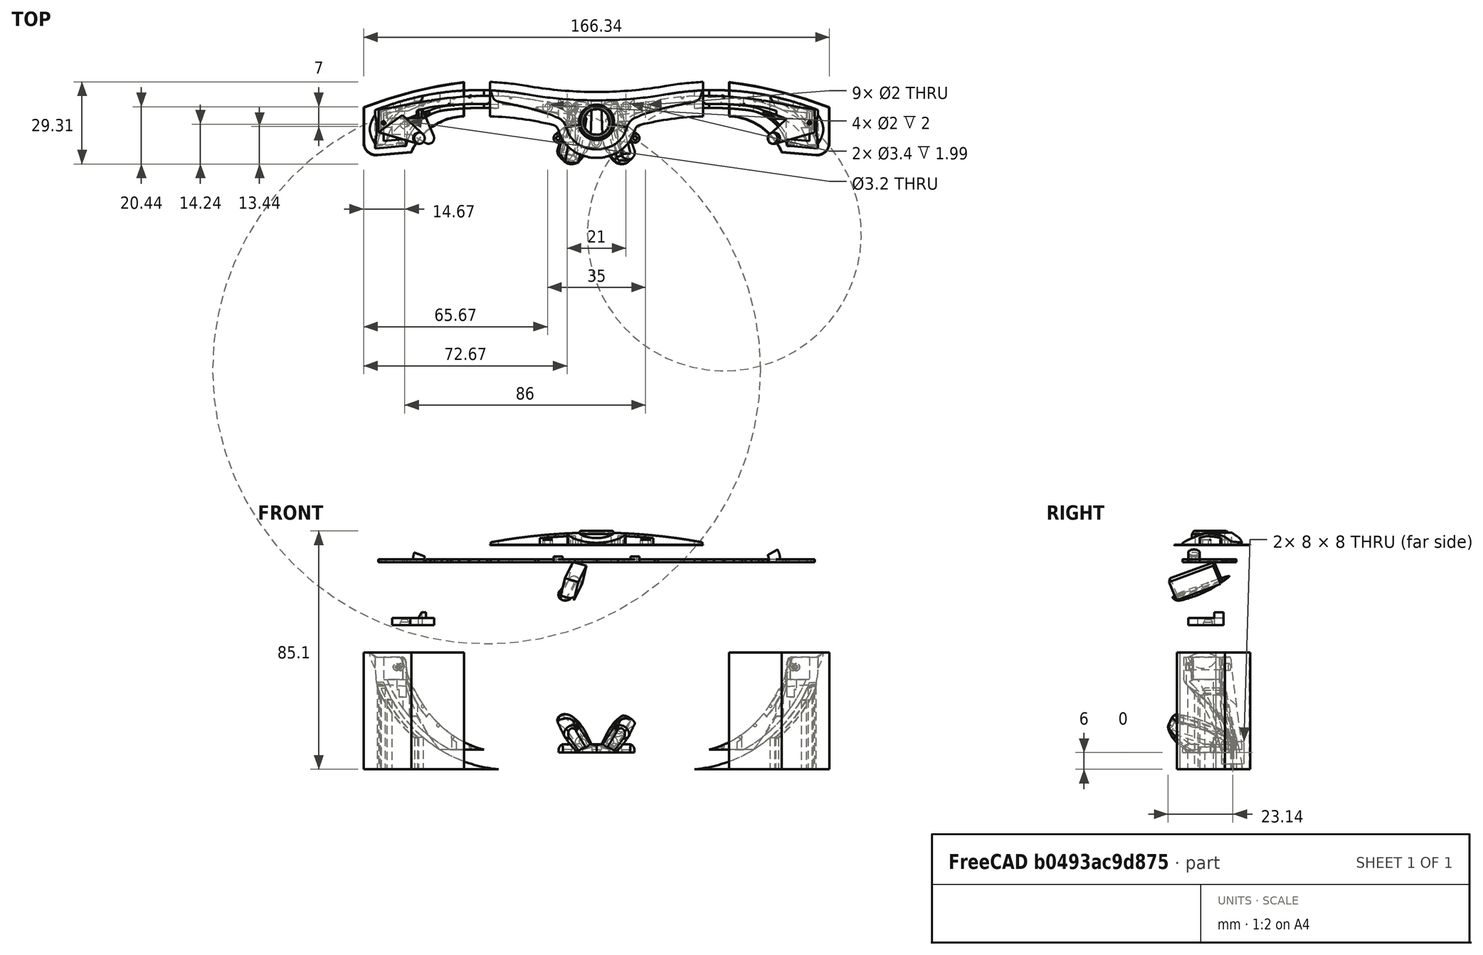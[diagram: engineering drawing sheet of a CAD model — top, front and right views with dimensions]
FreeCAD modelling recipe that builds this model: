
FCSTD DOCUMENT  (FreeCAD 0.14R3700 (Git))
Label: frame12
License: CC-BY 3.0
LicenseURL: http://creativecommons.org/licenses/by/3.0/
objects: Sketcher::SketchObject×44, Part::Extrusion×40, Part::MultiFuse×40, Part::Cut×33, Part::Box×23, Part::MultiCommon×16, Part::Sphere×14, Part::Cylinder×13, Part::FeaturePython×10, Part::Mirroring×9, Part::Loft×8, Part::Feature×7, Part::Fillet×7, PartDesign::Pad×6, Part::Offset×4, Mesh::Feature×4, PartDesign::Revolution×2, Part::Thickness×1
note: 285 computed .brp shape members not serialized (recipe doc carries the construction recipe); baked Part::Feature solids carry a one-line shape summary decoded from their .brp

FEATURE [Sketcher::SketchObject] Sketch001
  sketch-geometry (15):
    g0: ArcOfCircle CenterX=-40.8218 CenterY=-97.0566 CenterZ=0 NormalX=0 NormalY=0 NormalZ=1 Radius=107.874 StartAngle=1.32625 EndAngle=1.69394
    g1: ArcOfCircle CenterX=-42.1655 CenterY=-80.3985 CenterZ=0 NormalX=0 NormalY=0 NormalZ=1 Radius=97.5538 StartAngle=1.39785 EndAngle=1.92498
    g2: LineSegment [constr] StartX=-80 StartY=19.6499 StartZ=0 EndX=80 EndY=19.6499 EndZ=0
    g3: Circle [constr] CenterX=0 CenterY=6 CenterZ=0 NormalX=0 NormalY=0 NormalZ=1 Radius=5.2
    g4: GeomPoint [constr] X=-76 Y=11.1 Z=0
    g5: LineSegment StartX=0 StartY=13.5 StartZ=0 EndX=0 EndY=-4 EndZ=0
    g6: Circle [constr] CenterX=-7.5 CenterY=3.5 CenterZ=0 NormalX=0 NormalY=0 NormalZ=1 Radius=1.25
    g7: LineSegment [constr] StartX=-7.9694 StartY=13.5 StartZ=0 EndX=9.38441 EndY=13.5 EndZ=0
    g8: ArcOfCircle CenterX=-16.005 CenterY=2.39295 CenterZ=0 NormalX=0 NormalY=0 NormalZ=1 Radius=5.3743 StartAngle=0.264318 EndAngle=1.32625
    g9: ArcOfCircle CenterX=-0.822877 CenterY=6.50201 CenterZ=0 NormalX=0 NormalY=0 NormalZ=1 Radius=10.3541 StartAngle=3.40591 EndAngle=4.45086
    g10: ArcOfCircle CenterX=0.329777 CenterY=10.8084 CenterZ=0 NormalX=0 NormalY=0 NormalZ=1 Radius=14.8121 StartAngle=4.45086 EndAngle=4.69012
    g11: ArcOfCircle CenterX=1.76172e-06 CenterY=160.97 CenterZ=0 NormalX=0 NormalY=0 NormalZ=1 Radius=147.47 StartAngle=4.53944 EndAngle=4.71239
    g12: LineSegment StartX=-76 StartY=11.1 StartZ=0 EndX=-76 EndY=-3.4 EndZ=0
    g13: ArcOfCircle CenterX=-52.0663 CenterY=-6.2076 CenterZ=0 NormalX=0 NormalY=0 NormalZ=1 Radius=16.3313 StartAngle=1.69394 EndAngle=2.92806
    g14: LineSegment StartX=-76 StartY=-3.4 StartZ=0 EndX=-68.0267 EndY=-2.74684 EndZ=0
  constraints (44):
    c: Horizontal(g2)
    c: Distance(g2) = 160
    c: Symmetric(g2,g2,g-2)
    c: Radius(g3) = 5.2
    c: PointOnObject(g3,g-2)
    c: DistanceY(g-1,g3) = 6
    c: Vertical(g5)
    c: PointOnObject(g5,g-2)
    c: Distance(g5,g3) = 7.5
    c: Radius(g6) = 1.25
    c: Distance(g6,g5) = 7.5
    c: Horizontal(g7)
    c: PointOnObject(g5,g7)
    c: Coincident(g8,g0)
    c: Coincident(g9,g8)
    c: Tangent(g9,g8)
    c: Coincident(g10,g9)
    c: Tangent(g10,g9)
    c: Coincident(g10,g5)
    c: Coincident(g11,g1)
    c: Tangent(g11,g1)
    c: Tangent(g8,g0)
    c: Coincident(g1,g4)
    c: DistanceY(g12) = -14.5
    c: DistanceY(g5,g3) = 10
    c: Coincident(g1,g12)
    c: Coincident(g11,g5)
    c: Coincident(g13,g0)
    c: Tangent(g0,g13)
    c: DistanceX(g0) = -14.7038
    c: DistanceY(g0) = 7.60735
    c: Coincident(g14,g12)
    c: Coincident(g13,g14)
    c: Distance(g14) = 8
    c: DistanceX(g-2,g1) = -76
    c: DistanceY(g6,g3) = 2.5
    c: DistanceY(g1) = 15.7
    c: Tangent(g7,g11)
    c: DistanceX(g0) = -54.0724
    c: DistanceY(g0) = 10
    c: DistanceY(g9) = -3.5
    c: DistanceX(g9) = -3.5
    c: Vertical(g12)
    c: DistanceY(g12) = -3.4
FEATURE [Part::Extrusion] Extrude003
  Base = -> Sketch001
  Dir = (0,0,40)
  Solid = true
FEATURE [Sketcher::SketchObject] Sketch
  ExternalGeometry = -> [Extrude003]
  Placement = pos=(0,0,40) rot=(0,0,1;0rad)
  Support = -> Extrude003 [Face12]
  sketch-geometry (17):
    g0: ArcOfCircle CenterX=-41.618 CenterY=-95.1729 CenterZ=0 NormalX=0 NormalY=0 NormalZ=1 Radius=107.432 StartAngle=1.31635 EndAngle=1.68162
    g1: ArcOfCircle CenterX=-39.255 CenterY=-82.6924 CenterZ=0 NormalX=0 NormalY=0 NormalZ=1 Radius=97.8262 StartAngle=1.39348 EndAngle=1.70145
    g2: LineSegment [constr] StartX=-80 StartY=19.6499 StartZ=0 EndX=80 EndY=19.6499 EndZ=0
    g3: Circle [constr] CenterX=0 CenterY=6 CenterZ=0 NormalX=0 NormalY=0 NormalZ=1 Radius=5.2
    g4: LineSegment StartX=0 StartY=12 StartZ=0 EndX=0 EndY=-3 EndZ=0
    g5: Circle [constr] CenterX=-7.5 CenterY=4 CenterZ=0 NormalX=0 NormalY=0 NormalZ=1 Radius=1.25
    g6: ArcOfCircle CenterX=-16.4199 CenterY=1.71051 CenterZ=0 NormalX=0 NormalY=0 NormalZ=1 Radius=7.32535 StartAngle=0.257118 EndAngle=1.31635
    g7: ArcOfCircle CenterX=-1.30056 CenterY=5.68595 CenterZ=0 NormalX=0 NormalY=0 NormalZ=1 Radius=8.30788 StartAngle=3.39871 EndAngle=4.3949
    g8: ArcOfCircle CenterX=1.44145 CenterY=14.0305 CenterZ=0 NormalX=0 NormalY=0 NormalZ=1 Radius=17.0914 StartAngle=4.3949 EndAngle=4.62795
    g9: LineSegment StartX=-76 StartY=9.05149 StartZ=0 EndX=-76 EndY=-0.948515 EndZ=0
    g10: ArcOfCircle CenterX=-51.3984 CenterY=-7.28562 CenterZ=0 NormalX=0 NormalY=0 NormalZ=1 Radius=19.0022 StartAngle=1.68162 EndAngle=2.76947
    g11: LineSegment StartX=-76 StartY=-0.948515 StartZ=0 EndX=-69.1 EndY=-0.376553 EndZ=0
    g12: LineSegment StartX=-76 StartY=9.05149 StartZ=0 EndX=-69 EndY=9.63174 EndZ=0
    g13: ArcOfCircle CenterX=-45.6302 CenterY=-34.1756 CenterZ=0 NormalX=0 NormalY=0 NormalZ=1 Radius=48.8923 StartAngle=1.70145 EndAngle=2.01768
    g14: LineSegment StartX=-4 StartY=12 StartZ=0 EndX=0 EndY=12 EndZ=0
    g15: ArcOfCircle CenterX=-4.00001 CenterY=114.05 CenterZ=0 NormalX=0 NormalY=0 NormalZ=1 Radius=102.05 StartAngle=4.53508 EndAngle=4.71239
    g16: LineSegment StartX=-66.7595 StartY=9.91534 StartZ=0 EndX=-69 EndY=9.63174 EndZ=0
  constraints (51):
    c: Horizontal(g2)
    c: Distance(g2) = 160
    c: Symmetric(g2,g2,g-2)
    c: Radius(g3) = 5.2
    c: PointOnObject(g3,g-2)
    c: DistanceY(g-1,g3) = 6
    c: Vertical(g4)
    c: PointOnObject(g4,g-2)
    c: Distance(g4,g3) = 6
    c: Radius(g5) = 1.25
    c: Distance(g5,g4) = 7.5
    c: Coincident(g6,g0)
    c: Coincident(g7,g6)
    c: Tangent(g7,g6)
    c: Coincident(g8,g7)
    c: Tangent(g8,g7)
    c: Tangent(g6,g0)
    c: DistanceY(g9) = -10
    c: DistanceY(g4,g3) = 9
    c: Coincident(g10,g0)
    c: Tangent(g0,g10)
    c: Coincident(g11,g9)
    c: Coincident(g10,g11)
    c: Distance(g10,g-4) = 2.45
    c: Coincident(g12,g9)
    c: DistanceX(g0) = -14.576
    c: DistanceY(g0) = 8.8
    c: Coincident(g8,g4)
    c: DistanceY(g0) = 11.6
    c: Coincident(g13,g1)
    c: Tangent(g13,g1)
    c: PointOnObject(g9,g-3)
    c: PointOnObject(g9,g-3)
    c: DistanceX(g10) = -69.1
    c: DistanceY(g1) = 14.3
    c: DistanceX(g1) = -52
    c: Coincident(g15,g1)
    c: Coincident(g15,g14)
    c: Tangent(g15,g14)
    c: Horizontal(g14)
    c: Coincident(g14,g4)
    c: Tangent(g15,g1)
    c: DistanceX(g14) = -4
    c: DistanceY(g1) = 13.6
    c: DistanceX(g1) = -22
    c: DistanceX(g0) = -53.5
    c: Coincident(g16,g13)
    c: Coincident(g16,g12)
    c: Radius(g0) = 107.432
    c: DistanceX(g12) = -69
    c: Parallel(g12,g11)
FEATURE [Part::Extrusion] Extrude002
  Base = -> Sketch
  Dir = (0,0,-40)
  Solid = true
FEATURE [Sketcher::SketchObject] Sketch002
  Placement = pos=(0,-15,0) rot=(1,0,0;1.5708rad)
  sketch-geometry (12):
    g0: LineSegment StartX=0 StartY=40 StartZ=0 EndX=0 EndY=34 EndZ=0
    g1: LineSegment [constr] StartX=0 StartY=40 StartZ=0 EndX=0 EndY=0 EndZ=0
    g2: LineSegment [constr] StartX=-76 StartY=0 StartZ=0 EndX=-76 EndY=40 EndZ=0
    g3: LineSegment [constr] StartX=-60 StartY=34 StartZ=0 EndX=-60 EndY=29 EndZ=0
    g4: LineSegment StartX=-35 StartY=40 StartZ=0 EndX=0 EndY=40 EndZ=0
    g5: ArcOfCircle CenterX=-29.5232 CenterY=-9.43659 CenterZ=0 NormalX=0 NormalY=0 NormalZ=1 Radius=50 StartAngle=2.27585 EndAngle=2.76395
    g6: ArcOfCircle CenterX=-30.8281 CenterY=-2.13188 CenterZ=0 NormalX=0 NormalY=0 NormalZ=1 Radius=36.3719 StartAngle=1.68575 EndAngle=2.3997
    g7: ArcOfCircle CenterX=-27.7253 CenterY=-4.97584 CenterZ=0 NormalX=0 NormalY=0 NormalZ=1 Radius=40.5809 StartAngle=2.3997 EndAngle=3.01867
    g8: ArcOfCircle CenterX=-30.4815 CenterY=-8.31047 CenterZ=0 NormalX=0 NormalY=0 NormalZ=1 Radius=48.5213 StartAngle=1.66406 EndAngle=2.27585
    g9: LineSegment StartX=-35 StartY=34 StartZ=0 EndX=0 EndY=34 EndZ=0
    g10: LineSegment StartX=-76 StartY=0 StartZ=0 EndX=-68 EndY=0 EndZ=0
    g11: LineSegment StartX=-76 StartY=9 StartZ=0 EndX=-76 EndY=0 EndZ=0
  constraints (33):
    c: Distance(g0,g0) = 6
    c: Vertical(g1)
    c: Vertical(g2)
    c: Coincident(g1,g-1)
    c: DistanceY(g2) = 40
    c: PointOnObject(g0,g1)
    c: DistanceY(g3) = -5
    c: Vertical(g3)
    c: Distance(g4) = 35
    c: Coincident(g7,g6)
    c: Tangent(g7,g6)
    c: Horizontal(g4)
    c: Coincident(g4,g0)
    c: DistanceY(g-1,g0) = 40
    c: Vertical(g0)
    c: Coincident(g4,g8)
    c: DistanceX(g2) = -76
    c: Coincident(g8,g5)
    c: Tangent(g8,g5)
    c: Coincident(g9,g6)
    c: Coincident(g9,g0)
    c: Horizontal(g9)
    c: Equal(g9,g4)
    c: PointOnObject(g7,g-1)
    c: Radius(g5) = 50
    c: PointOnObject(g2,g-1)
    c: Coincident(g10,g2)
    c: Coincident(g10,g7)
    c: Distance(g10) = 8
    c: DistanceY(g5) = 9
    c: Coincident(g11,g5)
    c: Coincident(g11,g2)
    c: Vertical(g11)
FEATURE [Part::Extrusion] Extrude
  Base = -> Sketch002
  Dir = (0,40,0)
  Solid = true
FEATURE [Part::MultiCommon] Common001  label="trunk"
  Shapes = -> [Extrude,Extrude003]
FEATURE [Part::Extrusion] Extrude001
  Base = -> Sketch002
  Dir = (0,40,0)
  Placement = pos=(1,0,-1.5) rot=(0,0,1;0rad)
  Solid = true
FEATURE [Part::MultiCommon] Common  label="trunk inner"
  Shapes = -> [Extrude001,Extrude002]
FEATURE [Part::Cut] Cut  label="trunk002"
  Base = -> Common001
  Tool = -> Common
FEATURE [Sketcher::SketchObject] Sketch004
  Placement = pos=(-46.8224,0,73.5) rot=(0,-1,0;1.0472rad)
  sketch-geometry (3):
    g0: ArcOfCircle CenterX=-34.7524 CenterY=-32.9515 CenterZ=0 NormalX=0 NormalY=0 NormalZ=1 Radius=49.1722 StartAngle=1.79408 EndAngle=2.63591
    g1: LineSegment StartX=-77.7704 StartY=-9.13213 StartZ=0 EndX=-45.641 EndY=-9.13213 EndZ=0
    g2: LineSegment StartX=-45.641 StartY=15 StartZ=0 EndX=-45.641 EndY=-9.13213 EndZ=0
  constraints (8):
    c: Coincident(g1,g0)
    c: Horizontal(g1)
    c: Coincident(g2,g0)
    c: Coincident(g2,g1)
    c: Vertical(g2)
    c: DistanceX(g0) = -77.7704
    c: DistanceY(g0) = -9.13213
    c: DistanceY(g0) = 15
FEATURE [Part::Extrusion] Extrude005  label="sideCut"
  Base = -> Sketch004
  Dir = (30,0,0)
  Solid = true
FEATURE [Part::Box] Box  label="Cube002"
  Height = 21
  Length = 18
  Placement = pos=(-78,3.8,11) rot=(0,0,1;0rad)
  Width = 14
FEATURE [Part::Box] Box002  label="Cube022"
  Height = 13
  Length = 11.5
  Placement = pos=(-75,-1,8) rot=(0,0,1;0rad)
  Width = 8
FEATURE [Part::Box] Box003  label="Cube023"
  Height = 29
  Length = 17
  Placement = pos=(-75,-1.2,6) rot=(0,0,1;0rad)
  Width = 12
FEATURE [Part::Box] Box004  label="Cube017"
  Height = 15
  Length = 8
  Placement = pos=(-69.7,-0.95,-0.8) rot=(0,0,1;0rad)
  Width = 10
FEATURE [Part::Box] Box005  label="Cube032"
  Height = 15
  Length = 15
  Placement = pos=(-79.5,-0.95,-7) rot=(0,0,1;0rad)
  Width = 10
FEATURE [Part::Box] Box006  label="Cube033"
  Height = 12.5
  Length = 10
  Placement = pos=(-70.5,-0.95,-1) rot=(0,0,1;0rad)
  Width = 10
FEATURE [Part::MultiFuse] Fusion003
  Placement = pos=(-0.285398,6.6,0) rot=(0,0,1;0.087266rad)
  Shapes = -> [Box004,Box005,Box006]
FEATURE [Part::Cut] Cut010  label="trunk003"
  Base = -> Cut
  Tool = -> Fusion003
FEATURE [Sketcher::SketchObject] Sketch015
  Placement = pos=(-46.8224,0,71.5321) rot=(0,-1,0;1.0472rad)
  sketch-geometry (3):
    g0: ArcOfCircle CenterX=-32.5352 CenterY=-52.0195 CenterZ=0 NormalX=0 NormalY=0 NormalZ=1 Radius=62.8287 StartAngle=1.65242 EndAngle=2.37985
    g1: LineSegment StartX=-78 StartY=-8.65601 StartZ=0 EndX=-37.6576 EndY=-8.65601 EndZ=0
    g2: LineSegment StartX=-37.6576 StartY=10.6 StartZ=0 EndX=-37.6576 EndY=-8.65601 EndZ=0
  constraints (8):
    c: Coincident(g1,g0)
    c: Horizontal(g1)
    c: Coincident(g2,g0)
    c: Coincident(g2,g1)
    c: Vertical(g2)
    c: DistanceX(g0) = -37.6576
    c: DistanceY(g0) = 10.6
    c: DistanceX(g0) = -78
FEATURE [Part::Extrusion] Extrude008
  Base = -> Sketch015
  Dir = (20,0,0)
  Placement = pos=(0,1.5,0) rot=(0,0,1;0rad)
  Solid = true
FEATURE [Part::Extrusion] Extrude009
  Base = -> Sketch015
  Dir = (30,0,0)
  Solid = true
FEATURE [Part::MultiCommon] Common003
  Shapes = -> [Box003,Extrude008]
FEATURE [Part::MultiFuse] Fusion004  label="sideInner"
  Shapes = -> [Box002,Common003]
FEATURE [Part::MultiCommon] Common004  label="sideInner001"
  Shapes = -> [Fusion004,Common001]
FEATURE [Part::Box] Box007  label="Cube037"
  Height = 4
  Length = 9.3
  Placement = pos=(-8.3,-3,35) rot=(0,0,1;0rad)
  Width = 4
FEATURE [Part::Cylinder] Cylinder
  Angle = 360
  Height = 6.5
  Placement = pos=(-9,10,31) rot=(0,0,1;0rad)
  Radius = 1
FEATURE [Part::Box] Box008  label="Cube038"
  Height = 4
  Length = 4
  Placement = pos=(-13,10.5,35) rot=(0,0,1;0rad)
  Width = 2
FEATURE [Part::Cylinder] Cylinder001
  Angle = 360
  Height = 4
  Placement = pos=(-11,10.5,35) rot=(0,0,1;0rad)
  Radius = 2
FEATURE [Part::MultiFuse] Fusion005
  Placement = pos=(2,-0.5,0) rot=(0,0,1;0rad)
  Shapes = -> [Cylinder001,Box008]
FEATURE [Part::Cut] Cut011
  Base = -> Fusion005
  Placement = pos=(-1.5,1.2,0) rot=(0,0,1;0rad)
  Tool = -> Cylinder
FEATURE [Part::MultiCommon] Common005
  Shapes = -> [Box007,Common]
FEATURE [Part::Cylinder] Cylinder002
  Angle = 360
  Height = 12.5
  Placement = pos=(0,5.8,32) rot=(0,0,1;0rad)
  Radius = 5.3
FEATURE [Part::Box] Box009  label="Cube024"
  Height = 2
  Length = 8.4
  Placement = pos=(-4.2,1.6,32) rot=(0,0,1;0rad)
  Width = 8.4
FEATURE [Part::MultiFuse] Fusion006  label="camera"
  Shapes = -> [Cylinder002,Box009]
FEATURE [Part::MultiFuse] Fusion007  label="inner"
  Shapes = -> [Cut011,Common005]
FEATURE [Sketcher::SketchObject] Sketch016
  Placement = pos=(0,0,34) rot=(1,0,0;3.14159rad)
  sketch-geometry (7):
    g0: ArcOfCircle CenterX=-13.75 CenterY=0 CenterZ=0 NormalX=0 NormalY=0 NormalZ=1 Radius=1.6 StartAngle=1.51787 EndAngle=4.02214
    g1: LineSegment StartX=-14.7688 StartY=-1.23374 StartZ=0 EndX=-8.68396 EndY=-6.25827 EndZ=0
    g2: LineSegment StartX=-13.6654 StartY=1.59776 StartZ=0 EndX=-7.7 EndY=1.28174 EndZ=0
    g3: ArcOfCircle CenterX=-0.545251 CenterY=-6.72046 CenterZ=0 NormalX=0 NormalY=0 NormalZ=1 Radius=10.7343 StartAngle=1.51998 EndAngle=2.30034
    g4: ArcOfCircle CenterX=0 CenterY=-6 CenterZ=0 NormalX=0 NormalY=0 NormalZ=1 Radius=6 StartAngle=1.5708 EndAngle=3.18465
    g5: LineSegment StartX=-8.68396 StartY=-6.25827 StartZ=0 EndX=-5.99444 EndY=-6.25827 EndZ=0
    g6: LineSegment StartX=0 StartY=4 StartZ=0 EndX=0 EndY=0 EndZ=0
  constraints (21):
    c: DistanceY(g0) = 0
    c: Radius(g0) = 1.6
    c: DistanceX(g0) = -13.75
    c: Coincident(g1,g0)
    c: Coincident(g2,g0)
    c: Tangent(g2,g0)
    c: Tangent(g1,g0)
    c: Coincident(g3,g2)
    c: PointOnObject(g3,g-2)
    c: DistanceY(g3) = 4
    c: PointOnObject(g4,g-2)
    c: DistanceY(g4) = -6
    c: Radius(g4) = 6
    c: PointOnObject(g4,g-2)
    c: Coincident(g5,g1)
    c: Coincident(g5,g4)
    c: Horizontal(g5)
    c: Coincident(g6,g3)
    c: Coincident(g6,g-1)
    c: DistanceX(g2) = -7.7
    c: DistanceY(g2) = 1.28174
FEATURE [Part::Cylinder] Cylinder004
  Angle = 360
  Height = 2
  Placement = pos=(-13.75,0,34) rot=(0,0,1;0rad)
  Radius = 1.6
FEATURE [Part::Cylinder] Cylinder005
  Angle = 360
  Height = 4
  Placement = pos=(-13.75,0,32.6) rot=(0,0,1;0rad)
  Radius = 0.7
FEATURE [Part::Extrusion] Extrude010  label="right holder"
  Base = -> Sketch016
  Dir = (0,0,1)
  Solid = true
FEATURE [Part::MultiFuse] Fusion009  label="rightHolder"
  Shapes = -> [Extrude010,Cylinder004]
FEATURE [Part::Cut] Cut012  label="rightHolder001"
  Base = -> Fusion009
  Tool = -> Cylinder005
FEATURE [Part::Sphere] Sphere
  Angle1 = -90
  Angle2 = 90
  Angle3 = 360
  Placement = pos=(-51.3628,11.8412,28.4927) rot=(1,0,0;1.5708rad)
  Radius = 0.55
FEATURE [Part::Sphere] Sphere001
  Angle1 = -90
  Angle2 = 90
  Angle3 = 360
  Placement = pos=(-21.3095,10.3221,34.5) rot=(1,0,0;1.5708rad)
  Radius = 0.55
FEATURE [Part::Sphere] Sphere002
  Angle1 = -90
  Angle2 = 90
  Angle3 = 360
  Placement = pos=(-38.3844,12.2073,33.9575) rot=(1,0,0;1.5708rad)
  Radius = 0.55
FEATURE [Part::Sphere] Sphere003
  Angle1 = -90
  Angle2 = 90
  Angle3 = 360
  Placement = pos=(-30.6467,14.7543,34.5) rot=(1,0,0;1.5708rad)
  Radius = 0.55
FEATURE [Part::Sphere] Sphere004
  Angle1 = -90
  Angle2 = 90
  Angle3 = 360
  Placement = pos=(-45.0432,14.9736,31.8897) rot=(1,0,0;1.5708rad)
  Radius = 0.55
FEATURE [Part::Sphere] Sphere006
  Angle1 = -90
  Angle2 = 90
  Angle3 = 360
  Placement = pos=(-56.5763,13.5545,24.2608) rot=(1,0,0;1.5708rad)
  Radius = 0.55
FEATURE [Part::Sphere] Sphere007
  Angle1 = -90
  Angle2 = 90
  Angle3 = 360
  Placement = pos=(-62.1328,11.9954,17.4689) rot=(1,0,0;1.5708rad)
  Radius = 0.55
FEATURE [Part::Box] Box010  label="Cube015"
  Height = 8
  Length = 11
  Placement = pos=(-76.9115,-1.07712,-5.23794e-07) rot=(-0.030761,0.706774,0.70677;0.123394rad)
  Width = 10
FEATURE [Part::FeaturePython] Facebinder  # WARN: FeaturePython — macro-defined, semantics opaque (R4)
  Faces = -> [Common001]
FEATURE [Part::Extrusion] Extrude011  label="side"
  Base = -> Facebinder
  Dir = (-3,-1,0)
  Solid = true
FEATURE [Part::Cut] Cut013  label="side001"
  Base = -> Extrude011
  Tool = -> Extrude005
FEATURE [Part::Cut] Cut014  label="side002"
  Base = -> Extrude011
  Placement = pos=(1.2,-1,0) rot=(0,0,1;0rad)
  Tool = -> Extrude005
FEATURE [Part::MultiCommon] Common006
  Shapes = -> [Cut014,Box]
FEATURE [Sketcher::SketchObject] Sketch017
  Placement = pos=(-0.229946,2.807,0) rot=(0.998332,0.040823,0.040823;1.57247rad)
  sketch-geometry (4):
    g0: LineSegment StartX=-71.1534 StartY=16.0049 StartZ=0 EndX=-84.6914 EndY=16.0049 EndZ=0
    g1: LineSegment StartX=-84.6914 StartY=16.0049 StartZ=0 EndX=-84.6914 EndY=-1.48622 EndZ=0
    g2: LineSegment StartX=-84.6914 StartY=-1.48622 StartZ=0 EndX=-71.1534 EndY=-1.48622 EndZ=0
    g3: LineSegment StartX=-71.1534 StartY=-1.48622 StartZ=0 EndX=-71.1534 EndY=16.0049 EndZ=0
  constraints (8):
    c: Coincident(g0,g1)
    c: Coincident(g1,g2)
    c: Coincident(g2,g3)
    c: Coincident(g3,g0)
    c: Horizontal(g0)
    c: Horizontal(g2)
    c: Vertical(g1)
    c: Vertical(g3)
FEATURE [PartDesign::Pad] Pad001
  Length = 2
  Length2 = 100
  Placement = pos=(-0.229946,2.807,0) rot=(0.998332,0.040823,0.040823;1.57247rad)
  Sketch = -> Sketch017
  Type = 0
FEATURE [Sketcher::SketchObject] Sketch018
  Placement = pos=(-79,0,0) rot=(0.57735,-0.57735,-0.57735;2.0944rad)
  sketch-geometry (1):
    g0: Circle CenterX=-3.16726 CenterY=-1.78533 CenterZ=0 NormalX=0 NormalY=0 NormalZ=1 Radius=5.5
  constraints (1):
    c: Radius(g0) = 5.5
FEATURE [Sketcher::SketchObject] Sketch019
  Placement = pos=(-80,0,0) rot=(0.57735,-0.57735,-0.57735;2.0944rad)
  sketch-geometry (1):
    g0: Circle CenterX=-3.16726 CenterY=-1.78533 CenterZ=0 NormalX=0 NormalY=0 NormalZ=1 Radius=3.65
  constraints (1):
    c: Radius(g0) = 3.65
FEATURE [Sketcher::SketchObject] Sketch020
  Placement = pos=(-81,0,0) rot=(0.57735,-0.57735,-0.57735;2.0944rad)
  sketch-geometry (1):
    g0: Circle CenterX=-3.16726 CenterY=-1.78533 CenterZ=0 NormalX=0 NormalY=0 NormalZ=1 Radius=0.1
  constraints (1):
    c: Radius(g0) = 0.1
FEATURE [Sketcher::SketchObject] Sketch021
  Placement = pos=(-79,0,0) rot=(0.57735,-0.57735,-0.57735;2.0944rad)
  sketch-geometry (1):
    g0: Circle CenterX=-3.16726 CenterY=-1.78533 CenterZ=0 NormalX=0 NormalY=0 NormalZ=1 Radius=5.5
  constraints (1):
    c: Radius(g0) = 5.5
FEATURE [Part::Loft] Loft
  Closed = false
  Ruled = false
  Sections = -> [Sketch018,Sketch019,Sketch020]
  Solid = true
FEATURE [Part::Extrusion] Extrude012
  Base = -> Sketch021
  Dir = (1,0,0)
  Solid = true
FEATURE [Sketcher::SketchObject] Sketch022
  Placement = pos=(-78,0,0) rot=(0.57735,0.57735,0.57735;2.0944rad)
  Support = -> Extrude012 [Face3]
  sketch-geometry (6):
    g0: ArcOfCircle CenterX=3.40288 CenterY=31.0621 CenterZ=0 NormalX=0 NormalY=0 NormalZ=1 Radius=30.9554 StartAngle=4.58278 EndAngle=4.9085
    g1: LineSegment StartX=-2.49186 StartY=0.366288 StartZ=0 EndX=-7.74664 EndY=-10.0439 EndZ=0
    g2: LineSegment StartX=-7.74664 StartY=-10.0439 StartZ=0 EndX=15.6512 EndY=-10.0439 EndZ=0
    g3: LineSegment StartX=15.6512 StartY=-10.0439 StartZ=0 EndX=9.49468 EndY=0.7 EndZ=0
    g4: LineSegment StartX=9.49468 StartY=0.7 StartZ=0 EndX=9.43464 EndY=0.7 EndZ=0
    g5: LineSegment StartX=-0.597926 StartY=0.366288 StartZ=0 EndX=-2.49186 EndY=0.366288 EndZ=0
  constraints (11):
    c: Coincident(g2,g1)
    c: Horizontal(g2)
    c: Coincident(g3,g2)
    c: Coincident(g3,g4)
    c: Coincident(g0,g4)
    c: Horizontal(g4)
    c: Coincident(g0,g5)
    c: Coincident(g1,g5)
    c: Horizontal(g5)
    c: DistanceY(g0) = 0.366288
    c: DistanceY(g0) = 0.7
FEATURE [Part::Extrusion] Extrude013
  Base = -> Sketch022
  Dir = (-3,0,-2)
  Solid = true
FEATURE [Part::MultiFuse] Fusion011  label="sideDisc"
  Shapes = -> [Extrude012,Loft]
FEATURE [Part::Cut] Cut016  label="sideDisc001"
  Base = -> Fusion011
  Placement = pos=(0,0,0.2) rot=(0,0,1;0rad)
  Tool = -> Extrude013
FEATURE [Part::Cylinder] Cylinder013
  Angle = 360
  Height = 20
  Placement = pos=(-71.2,14,3) rot=(1,0,0;1.5708rad)
  Radius = 0.6
FEATURE [Part::Cylinder] Cylinder014
  Angle = 360
  Height = 3.7
  Placement = pos=(-71.2,14,3) rot=(1,0,0;1.5708rad)
  Radius = 1.25
FEATURE [Part::Cylinder] Cylinder015
  Angle = 360
  Height = 3.7
  Placement = pos=(-71.2,-2.2,3) rot=(1,0,0;1.5708rad)
  Radius = 1.25
FEATURE [Part::MultiFuse] Fusion014
  Placement = pos=(0.6,6.7,0.5) rot=(0,0,1;0.087266rad)
  Shapes = -> [Cylinder013,Cylinder014,Cylinder015]
FEATURE [Sketcher::SketchObject] Sketch023
  Placement = pos=(-77.783,8.88483,0.000119934) rot=(0,0.708449,0.705762;3.26493rad)
  sketch-geometry (3):
    g0: ArcOfCircle CenterX=-58.3252 CenterY=-8.18917 CenterZ=0 NormalX=0 NormalY=0 NormalZ=1 Radius=50.9248 StartAngle=0.153613 EndAngle=0.573611
    g1: LineSegment StartX=-15.551 StartY=19.4461 StartZ=0 EndX=-15.6541 EndY=-1.4654 EndZ=0
    g2: LineSegment StartX=-15.6541 StartY=-1.4654 StartZ=0 EndX=-8 EndY=-0.397193 EndZ=0
  constraints (5):
    c: Coincident(g1,g0)
    c: Coincident(g2,g1)
    c: Coincident(g2,g0)
    c: DistanceX(g0) = -8
    c: DistanceY(g0) = -0.397193
FEATURE [Part::Cut] Cut017  label="coverFace001"
  Base = -> Common
  Tool = -> Common001
FEATURE [Part::Box] Box011  label="Cube039"
  Height = 27
  Length = 10
  Placement = pos=(-69.7,-1,-19) rot=(0,0,1;0rad)
  Width = 18
FEATURE [Part::Cut] Cut018  label="coverFace002"
  Base = -> Cut017
  Tool = -> Box011
FEATURE [Part::FeaturePython] Facebinder002  # WARN: FeaturePython — macro-defined, semantics opaque (R4)
  Faces = -> [Cut018]
FEATURE [Part::Offset] Offset  label="coverFace003"
  Fill = false
  Intersection = false
  Join = 0
  Mode = 0
  SelfIntersection = false
  Source = -> Facebinder002
  Value = 0.5
FEATURE [Mesh::Feature] coverFlat
FEATURE [Mesh::Feature] coverFace  label="coverFace004"
FEATURE [Part::Feature] Shape  label="coverFace005"
  shape: bbox 63.93 x 18.13 x 20.06 mm, 45 faces, 0 solids (baked)
FEATURE [Part::Sphere] Sphere008
  Angle1 = -90
  Angle2 = 90
  Angle3 = 360
  Placement = pos=(-68.1046,11.9916,34.4996) rot=(1,0,0;1.5708rad)
  Radius = 0.6
FEATURE [Part::Sphere] Sphere010
  Angle1 = -90
  Angle2 = 90
  Angle3 = 360
  Placement = pos=(-59.3144,13.552,34.4996) rot=(1,0,0;1.5708rad)
  Radius = 0.6
FEATURE [Part::Sphere] Sphere011
  Angle1 = -90
  Angle2 = 90
  Angle3 = 360
  Placement = pos=(-52.5915,11.8406,34.4997) rot=(1,0,0;1.5708rad)
  Radius = 0.6
FEATURE [Part::Sphere] Sphere012
  Angle1 = -90
  Angle2 = 90
  Angle3 = 360
  Placement = pos=(-45.4082,14.9736,34.4998) rot=(1,0,0;1.5708rad)
  Radius = 0.6
FEATURE [Part::Sphere] Sphere013
  Angle1 = -90
  Angle2 = 90
  Angle3 = 360
  Placement = pos=(-38.428,12.2073,34.4998) rot=(1,0,0;1.5708rad)
  Radius = 0.6
FEATURE [Part::Sphere] Sphere014
  Angle1 = -90
  Angle2 = 90
  Angle3 = 360
  Placement = pos=(-30.6467,14.7543,34.5) rot=(1,0,0;1.5708rad)
  Radius = 0.6
FEATURE [Part::Sphere] Sphere015
  Angle1 = -90
  Angle2 = 90
  Angle3 = 360
  Placement = pos=(-21.3095,10.3221,34.5) rot=(1,0,0;1.5708rad)
  Radius = 0.6
FEATURE [Part::Extrusion] Extrude017  label="coverBent"
  Base = -> Facebinder002
  Dir = (-0.5,0,1.2)
  Solid = true
FEATURE [Part::Cylinder] Cylinder017
  Angle = 360
  Height = 10
  Placement = pos=(-51,15,24.4) rot=(0,0,1;0rad)
  Radius = 1
FEATURE [Part::Cylinder] Cylinder018
  Angle = 360
  Height = 6.5
  Placement = pos=(-44,11.9,31) rot=(0,0,1;0rad)
  Radius = 1
FEATURE [Part::Cylinder] Cylinder020
  Angle = 360
  Height = 6.5
  Placement = pos=(-37,15.5,32.5) rot=(0,0,1;0rad)
  Radius = 1
FEATURE [Sketcher::SketchObject] Sketch024
  Placement = pos=(0,0,40) rot=(1,0,0;3.14159rad)
  sketch-geometry (7):
    g0: ArcOfCircle CenterX=-8.39919 CenterY=-3.55195 CenterZ=0 NormalX=0 NormalY=0 NormalZ=1 Radius=2 StartAngle=2.9597 EndAngle=4.53987
    g1: ArcOfCircle CenterX=-9 CenterY=-7 CenterZ=0 NormalX=0 NormalY=0 NormalZ=1 Radius=1.5 StartAngle=4.83447 EndAngle=7.68147
    g2: LineSegment StartX=-10.3662 StartY=-3.19017 StartZ=0 EndX=-9.72761 EndY=0.281771 EndZ=0
    g3: LineSegment StartX=-20.2562 StartY=-10.0838 StartZ=0 EndX=-20.2562 EndY=0.281771 EndZ=0
    g4: LineSegment StartX=-20.2562 StartY=0.281771 StartZ=0 EndX=-9.72761 EndY=0.281771 EndZ=0
    g5: LineSegment StartX=-8.81733 StartY=-8.48884 StartZ=0 EndX=-17.2797 EndY=-9.52713 EndZ=0
    g6: ArcOfCircle CenterX=-14.3417 CenterY=-33.4726 CenterZ=0 NormalX=0 NormalY=0 NormalZ=1 Radius=24.125 StartAngle=1.69288 EndAngle=1.81848
  constraints (17):
    c: Radius(g0) = 2
    c: Coincident(g1,g0)
    c: Tangent(g1,g0)
    c: Coincident(g2,g0)
    c: Tangent(g2,g0)
    c: Vertical(g3)
    c: Coincident(g4,g3)
    c: Coincident(g4,g2)
    c: Horizontal(g4)
    c: Radius(g1) = 1.5
    c: Coincident(g5,g1)
    c: Tangent(g5,g1)
    c: DistanceX(g1) = -9
    c: DistanceY(g1) = -7
    c: Coincident(g6,g5)
    c: Tangent(g6,g5)
    c: Coincident(g3,g6)
FEATURE [Part::Extrusion] Extrude018  label="capCut"
  Base = -> Sketch024
  Dir = (0,0,5)
  Solid = true
FEATURE [Sketcher::SketchObject] Sketch025
  Placement = pos=(0,9.80138,40) rot=(0,0,1;0rad)
  sketch-geometry (12):
    g0: LineSegment StartX=-38 StartY=7.85704 StartZ=0 EndX=-37.0984 EndY=5.08436 EndZ=0
    g1: LineSegment StartX=-35.0047 StartY=3.21824 StartZ=0 EndX=-28.5152 EndY=1.90583 EndZ=0
    g2: LineSegment StartX=-20.9146 StartY=0.0008774 StartZ=0 EndX=-17.3315 EndY=-1.07462 EndZ=0
    g3: ArcOfCircle CenterX=-34.4533 CenterY=5.94447 CenterZ=0 NormalX=0 NormalY=0 NormalZ=1 Radius=2.78142 StartAngle=3.45598 EndAngle=4.51284
    g4: ArcOfCircle CenterX=-45.3938 CenterY=-81.5532 CenterZ=0 NormalX=0 NormalY=0 NormalZ=1 Radius=85.1487 StartAngle=1.27919 EndAngle=1.37125
    g5: GeomPoint [constr] X=-23.0911 Y=4.12523 Z=0
    g6: LineSegment StartX=-10.4688 StartY=-7.9903 StartZ=0 EndX=-10.4688 EndY=-16.0473 EndZ=0
    g7: LineSegment StartX=-38 StartY=7.85704 StartZ=0 EndX=0 EndY=7.85704 EndZ=0
    g8: LineSegment StartX=0 StartY=7.85704 StartZ=0 EndX=0 EndY=1.19862 EndZ=0
    g9: LineSegment StartX=-10.4688 StartY=-16.0473 StartZ=0 EndX=0 EndY=-16.0473 EndZ=0
    g10: LineSegment StartX=0 StartY=1.19862 StartZ=0 EndX=0 EndY=-16.0473 EndZ=0
    g11: ArcOfCircle CenterX=-19.7599 CenterY=-10.3474 CenterZ=0 NormalX=0 NormalY=0 NormalZ=1 Radius=9.58548 StartAngle=0.248451 EndAngle=1.31467
  constraints (19):
    c: Tangent(g0,g3)
    c: Tangent(g1,g3)
    c: Tangent(g1,g4)
    c: Tangent(g2,g4)
    c: PointOnObject(g8,g-2)
    c: PointOnObject(g10,g-2)
    c: Vertical(g6)
    c: Coincident(g7,g0)
    c: Horizontal(g7)
    c: Coincident(g8,g7)
    c: Vertical(g8)
    c: Coincident(g9,g6)
    c: Horizontal(g9)
    c: Vertical(g10)
    c: Coincident(g9,g10)
    c: Coincident(g11,g2)
    c: Coincident(g6,g11)
    c: Coincident(g10,g8)
    c: Distance(g7) = 38
FEATURE [Part::Extrusion] Extrude019  label="cap"
  Base = -> Sketch025
  Dir = (0,0,10)
  Solid = true
FEATURE [Sketcher::SketchObject] Sketch026
  Placement = pos=(0,-15,0) rot=(1,0,0;1.5708rad)
  sketch-geometry (5):
    g0: ArcOfCircle CenterX=0.000183054 CenterY=-165.538 CenterZ=0 NormalX=0 NormalY=0 NormalZ=1 Radius=208.038 StartAngle=1.5708 EndAngle=1.75449
    g1: LineSegment [constr] StartX=-37.2105 StartY=42.5 StartZ=0 EndX=1.0349 EndY=42.5 EndZ=0
    g2: LineSegment StartX=0 StartY=38 StartZ=0 EndX=0 EndY=42.5 EndZ=0
    g3: LineSegment StartX=-38 StartY=39 StartZ=0 EndX=-38 EndY=38 EndZ=0
    g4: LineSegment StartX=-38 StartY=38 StartZ=0 EndX=0 EndY=38 EndZ=0
  constraints (15):
    c: Horizontal(g1)
    c: PointOnObject(g0,g1)
    c: Tangent(g1,g0)
    c: PointOnObject(g0,g-2)
    c: Coincident(g2,g0)
    c: PointOnObject(g2,g-2)
    c: Coincident(g3,g0)
    c: Vertical(g3)
    c: Coincident(g4,g3)
    c: Horizontal(g4)
    c: Coincident(g4,g2)
    c: DistanceY(g3) = -1
    c: DistanceY(g2) = 38
    c: DistanceX(g0) = -38
    c: Distance(g2) = 4.5
FEATURE [Part::Extrusion] Extrude020
  Base = -> Sketch026
  Dir = (0,40,0)
  Placement = pos=(0,0,2) rot=(0,0,1;0rad)
  Solid = true
FEATURE [Part::Box] Box015  label="Cube020"
  Height = 10
  Length = 10
  Placement = pos=(0,-4,40) rot=(0,0,1;0rad)
  Width = 18
FEATURE [Part::Cylinder] Cylinder024
  Angle = 360
  Height = 7.7
  Placement = pos=(0,6,42) rot=(0,0,1;0rad)
  Radius = 4.6
FEATURE [Sketcher::SketchObject] Sketch027
  Placement = pos=(0,0,44.1) rot=(1,0,0;3.14159rad)
  sketch-geometry (1):
    g0: Circle CenterX=0 CenterY=-6 CenterZ=0 NormalX=0 NormalY=0 NormalZ=1 Radius=5.8
  constraints (3):
    c: DistanceY(g0) = -6
    c: PointOnObject(g0,g-2)
    c: Radius(g0) = 5.8
FEATURE [Sketcher::SketchObject] Sketch028
  Placement = pos=(0,0,43) rot=(1,0,0;3.14159rad)
  sketch-geometry (1):
    g0: Circle CenterX=0 CenterY=-6 CenterZ=0 NormalX=0 NormalY=0 NormalZ=1 Radius=6.5
  constraints (3):
    c: DistanceY(g0) = -6
    c: PointOnObject(g0,g-2)
    c: Radius(g0) = 6.5
FEATURE [Sketcher::SketchObject] Sketch029
  Placement = pos=(0,0,41) rot=(1,0,0;3.14159rad)
  sketch-geometry (1):
    g0: Circle CenterX=0 CenterY=-6 CenterZ=0 NormalX=0 NormalY=0 NormalZ=1 Radius=6.5
  constraints (3):
    c: DistanceY(g0) = -6
    c: PointOnObject(g0,g-2)
    c: Radius(g0) = 6.5
FEATURE [Part::Loft] Loft001  label="hat"
  Closed = false
  Ruled = true
  Sections = -> [Sketch029,Sketch028,Sketch027]
  Solid = true
FEATURE [Part::Cut] Cut023  label="hat001"
  Base = -> Loft001
  Tool = -> Cylinder024
FEATURE [Part::Cut] Cut022  label="hat002"
  Base = -> Cut023
  Placement = pos=(0,-0.2,1) rot=(0,0,1;0rad)
  Tool = -> Box015
FEATURE [Sketcher::SketchObject] Sketch032
  Placement = pos=(0,0,42) rot=(1,0,0;3.14159rad)
  sketch-geometry (1):
    g0: Circle CenterX=-17.5 CenterY=-11.2 CenterZ=0 NormalX=0 NormalY=0 NormalZ=1 Radius=1
  constraints (3):
    c: Radius(g0) = 1
    c: DistanceX(g0) = -17.5
    c: DistanceY(g0) = -11.2
FEATURE [Sketcher::SketchObject] Sketch030
  Placement = pos=(0,0,38.5) rot=(1,0,0;3.14159rad)
  sketch-geometry (1):
    g0: Circle CenterX=-17.5 CenterY=-11.2 CenterZ=0 NormalX=0 NormalY=0 NormalZ=1 Radius=1.6
  constraints (3):
    c: Radius(g0) = 1.6
    c: DistanceX(g0) = -17.5
    c: DistanceY(g0) = -11.2
FEATURE [Sketcher::SketchObject] Sketch031
  Placement = pos=(0,0,39.5) rot=(1,0,0;3.14159rad)
  sketch-geometry (1):
    g0: Circle CenterX=-17.5 CenterY=-11.2 CenterZ=0 NormalX=0 NormalY=0 NormalZ=1 Radius=1
  constraints (3):
    c: Radius(g0) = 1
    c: DistanceX(g0) = -17.5
    c: DistanceY(g0) = -11.2
FEATURE [Part::Loft] Loft002
  Closed = false
  Ruled = true
  Sections = -> [Sketch030,Sketch031,Sketch032]
  Solid = true
FEATURE [Part::Loft] Loft003
  Closed = false
  Placement = pos=(10,-7,0) rot=(0,0,1;0rad)
  Ruled = true
  Sections = -> [Sketch030,Sketch031,Sketch032]
  Solid = true
FEATURE [Part::Extrusion] Extrude022
  Base = -> Sketch026
  Dir = (0,40,0)
  Placement = pos=(0,0,1) rot=(0,0,1;0rad)
  Solid = true
FEATURE [Part::MultiCommon] Common011  label="capCut001"
  Shapes = -> [Extrude022,Extrude018]
FEATURE [Sketcher::SketchObject] Sketch033
  Placement = pos=(0,0,14) rot=(1,0,0;3.14159rad)
  sketch-geometry (9):
    g0: ArcOfCircle CenterX=-60 CenterY=0 CenterZ=0 NormalX=0 NormalY=0 NormalZ=1 Radius=2 StartAngle=5.88109 EndAngle=8.36318
    g1: LineSegment StartX=-58.1595 StartY=-0.782691 StartZ=0 EndX=-62.3124 EndY=-10.5482 EndZ=0
    g2: LineSegment [constr] StartX=-72.7253 StartY=6.64977 StartZ=0 EndX=-75.9479 EndY=-16.9476 EndZ=0
    g3: LineSegment StartX=-72.9323 StartY=-1.34066 StartZ=0 EndX=-72.9323 EndY=-7.26835 EndZ=0
    g4: LineSegment StartX=-60.9749 StartY=1.74627 StartZ=0 EndX=-66.5041 EndY=-1.34066 EndZ=0
    g5: LineSegment StartX=-72.9323 StartY=-1.34066 StartZ=0 EndX=-66.5041 EndY=-1.34066 EndZ=0
    g6: LineSegment StartX=-63.7165 StartY=-7.26835 StartZ=0 EndX=-72.9323 EndY=-7.26835 EndZ=0
    g7: LineSegment StartX=-62.3124 StartY=-10.5482 StartZ=0 EndX=-63.7165 EndY=-10.5482 EndZ=0
    g8: LineSegment StartX=-63.7165 StartY=-7.26835 StartZ=0 EndX=-63.7165 EndY=-10.5482 EndZ=0
  constraints (19):
    c: DistanceX(g0) = -60
    c: Radius(g0) = 2
    c: Tangent(g4,g0)
    c: Vertical(g3)
    c: Coincident(g0,g1)
    c: Coincident(g0,g4)
    c: Tangent(g1,g0)
    c: Horizontal(g5)
    c: Coincident(g5,g3)
    c: Coincident(g6,g3)
    c: Horizontal(g6)
    c: PointOnObject(g0,g-1)
    c: DistanceX(g6) = -63.7165
    c: Coincident(g7,g1)
    c: Coincident(g8,g6)
    c: Coincident(g8,g7)
    c: Vertical(g8)
    c: Horizontal(g7)
    c: Coincident(g5,g4)
FEATURE [Part::Extrusion] Extrude023  label="left holder"
  Base = -> Sketch033
  Dir = (0,0,-2.5)
  Solid = true
FEATURE [Part::Cut] Cut029  label="side003"
  Base = -> Cut013
  Tool = -> Common006
FEATURE [Part::Box] Box018  label="Cube036"
  Height = 53
  Length = 48
  Placement = pos=(-83,-8,40) rot=(0,0,1;0rad)
  Width = 30
FEATURE [Part::Loft] Loft005
  Closed = false
  Placement = pos=(-51,-6.2,-26) rot=(0,0,1;0rad)
  Ruled = true
  Sections = -> [Sketch030,Sketch031,Sketch032]
  Solid = true
FEATURE [Part::Cylinder] Cylinder025
  Angle = 360
  Height = 1
  Placement = pos=(-68.5,5,11.5) rot=(0,0,1;0rad)
  Radius = 1.6
FEATURE [Part::MultiFuse] Fusion038
  Shapes = -> [Loft005,Cylinder025]
FEATURE [Sketcher::SketchObject] Sketch036
  Placement = pos=(-0.492409,5.62826,0) rot=(-0.030858,0.70677,0.70677;3.20329rad)
  sketch-geometry (4):
    g0: ArcOfCircle CenterX=-27.9195 CenterY=-11.9603 CenterZ=0 NormalX=0 NormalY=0 NormalZ=1 Radius=96.8673 StartAngle=0.118834 EndAngle=0.209046
    g1: LineSegment StartX=66.8389 StartY=8.14222 StartZ=0 EndX=62.9985 EndY=6.61232 EndZ=0
    g2: LineSegment StartX=62.9985 StartY=6.61232 StartZ=0 EndX=63.2458 EndY=-3.45557 EndZ=0
    g3: LineSegment StartX=63.2458 StartY=-3.45557 StartZ=0 EndX=68.2646 EndY=-0.476282 EndZ=0
  constraints (6):
    c: Coincident(g1,g0)
    c: Coincident(g2,g1)
    c: Coincident(g3,g2)
    c: Coincident(g3,g0)
    c: DistanceX(g0) = 68.2646
    c: DistanceY(g0) = -0.476282
FEATURE [PartDesign::Pad] Pad002
  Length = 5
  Length2 = 100
  Placement = pos=(-0.492409,5.62826,0) rot=(-0.030858,0.70677,0.70677;3.20329rad)
  Reversed = true
  Sketch = -> Sketch036
  Type = 0
FEATURE [Sketcher::SketchObject] Sketch037
  ExternalGeometry = -> [Extrude023]
  Placement = pos=(0,0,14) rot=(0,0,1;0rad)
  Support = -> Extrude023 [Face9]
  sketch-geometry (4):
    g0: LineSegment StartX=-62.3124 StartY=10.5482 StartZ=0 EndX=-60.9067 EndY=7.24257 EndZ=0
    g1: LineSegment StartX=-62.3124 StartY=10.5482 StartZ=0 EndX=-63.7165 EndY=10.5482 EndZ=0
    g2: LineSegment StartX=-63.7165 StartY=10.5482 StartZ=0 EndX=-63.7165 EndY=7.24257 EndZ=0
    g3: LineSegment StartX=-63.7165 StartY=7.24257 StartZ=0 EndX=-60.9067 EndY=7.24257 EndZ=0
  constraints (11):
    c: Coincident(g1,g0)
    c: Coincident(g2,g1)
    c: Coincident(g0,g3)
    c: Horizontal(g3)
    c: Coincident(g2,g3)
    c: Vertical(g2)
    c: PointOnObject(g0,g-3)
    c: Horizontal(g1)
    c: Coincident(g1,g-4)
    c: Coincident(g0,g1)
    c: Coincident(g0,g-3)
FEATURE [Part::Extrusion] Extrude028
  Base = -> Sketch037
  Dir = (0,0,2)
  Solid = true
FEATURE [Part::Cut] Cut037  label="leftHolderCoverStop"
  Base = -> Extrude028
  Tool = -> Common001
FEATURE [Sketcher::SketchObject] Sketch038
  Placement = pos=(0,0,0) rot=(0.57735,0.57735,0.57735;2.0944rad)
  sketch-geometry (4):
    g0: ArcOfCircle CenterX=13.1942 CenterY=11.3517 CenterZ=0 NormalX=0 NormalY=0 NormalZ=1 Radius=34.1544 StartAngle=1.71935 EndAngle=2.13057
    g1: LineSegment StartX=-4.94148 StartY=40.2933 StartZ=0 EndX=-4.94148 EndY=46.3782 EndZ=0
    g2: LineSegment StartX=-4.94148 StartY=46.3782 StartZ=0 EndX=8.13928 EndY=46.3782 EndZ=0
    g3: LineSegment StartX=8.13928 StartY=46.3782 StartZ=0 EndX=8.13928 EndY=45.1299 EndZ=0
  constraints (9):
    c: Coincident(g1,g0)
    c: Vertical(g1)
    c: Coincident(g2,g1)
    c: Horizontal(g2)
    c: Coincident(g3,g2)
    c: Coincident(g3,g0)
    c: Vertical(g3)
    c: DistanceX(g0) = -4.94148
    c: DistanceY(g0) = 40.2933
FEATURE [Part::Extrusion] Extrude029
  Base = -> Sketch038
  Dir = (-20,0,0)
  Solid = true
FEATURE [Sketcher::SketchObject] Sketch039
  Placement = pos=(-20.2562,0,0) rot=(0.57735,-0.57735,-0.57735;2.0944rad)
  Support = -> Common011 [Face6]
  sketch-geometry (4):
    g0: ArcOfCircle CenterX=-7.02145 CenterY=27.5743 CenterZ=0 NormalX=0 NormalY=0 NormalZ=1 Radius=15.8627 StartAngle=0.824454 EndAngle=1.46672
    g1: LineSegment StartX=-5.37356 StartY=43.3512 StartZ=0 EndX=-5.37356 EndY=45.873 EndZ=0
    g2: LineSegment StartX=3.74867 StartY=39.2204 StartZ=0 EndX=3.74867 EndY=45.873 EndZ=0
    g3: LineSegment StartX=-5.37356 StartY=45.873 StartZ=0 EndX=3.74867 EndY=45.873 EndZ=0
  constraints (9):
    c: Coincident(g1,g0)
    c: Vertical(g1)
    c: Coincident(g2,g0)
    c: Vertical(g2)
    c: Coincident(g3,g1)
    c: Coincident(g3,g2)
    c: Horizontal(g3)
    c: DistanceX(g0) = 3.74867
    c: DistanceY(g0) = 39.2204
FEATURE [Part::Extrusion] Extrude030
  Base = -> Sketch039
  Dir = (20,0,0)
  Solid = true
FEATURE [Part::Cut] Cut039  label="capCut002"
  Base = -> Common011
  Tool = -> Extrude030
FEATURE [Part::MultiFuse] Fusion044  label="capCut003"
  Shapes = -> [Cut039,Loft003,Loft002,Fusion006]
FEATURE [Sketcher::SketchObject] Sketch040
  Placement = pos=(-0.229946,2.807,0) rot=(0.998332,0.040823,0.040823;1.57247rad)
  sketch-geometry (5):
    g0: ArcOfCircle CenterX=-19.8299 CenterY=0.328479 CenterZ=0 NormalX=0 NormalY=0 NormalZ=1 Radius=59.348 StartAngle=2.9877 EndAngle=3.15201
    g1: LineSegment StartX=-88.7398 StartY=11.366 StartZ=0 EndX=-88.7398 EndY=-0.289708 EndZ=0
    g2: LineSegment StartX=-88.7398 StartY=-0.289708 StartZ=0 EndX=-79.1747 EndY=-0.289708 EndZ=0
    g3: ArcOfCircle CenterX=-68.1556 CenterY=7.8248 CenterZ=0 NormalX=0 NormalY=0 NormalZ=1 Radius=10.4444 StartAngle=2.57089 EndAngle=2.9877
    g4: LineSegment StartX=-88.7398 StartY=11.366 StartZ=0 EndX=-76.9447 EndY=13.467 EndZ=0
  constraints (9):
    c: Vertical(g1)
    c: Coincident(g2,g1)
    c: Coincident(g2,g0)
    c: Horizontal(g2)
    c: DistanceY(g0) = -0.289708
    c: Coincident(g3,g0)
    c: Tangent(g3,g0)
    c: Coincident(g4,g1)
    c: Coincident(g4,g3)
FEATURE [Part::Extrusion] Extrude031
  Base = -> Sketch040
  Dir = (0,20,0)
  Placement = pos=(0,-1,0) rot=(0,0,1;0rad)
  Solid = true
FEATURE [Part::Cut] Cut041  label="side004"
  Base = -> Cut029
  Tool = -> Extrude031
FEATURE [Part::MultiFuse] Fusion  label="side005"
  Shapes = -> [Cut041,Cut016]
FEATURE [Part::Cut] Cut042  label="side006"
  Base = -> Fusion
  Tool = -> Pad001
FEATURE [Part::MultiFuse] Fusion047  label="coverSupport"
  Shapes = -> [Cylinder017,Cylinder018,Cylinder020]
FEATURE [Part::MultiCommon] Common013  label="coverSupport001"
  Shapes = -> [Common001,Fusion047]
FEATURE [Part::Cut] Cut043  label="coverSupport002"
  Base = -> Common013
  Tool = -> Extrude017
FEATURE [Part::MultiFuse] Fusion049  label="leftHolder"
  Shapes = -> [Cut037,Extrude023]
FEATURE [Part::Cut] Cut044  label="leftHolder001"
  Base = -> Fusion049
  Tool = -> Fusion038
FEATURE [Part::FeaturePython] Facebinder005  # WARN: FeaturePython — macro-defined, semantics opaque (R4)
  Faces = -> [Cut010]
FEATURE [Part::Extrusion] Extrude034
  Base = -> Facebinder005
  Dir = (0,0,40)
  Solid = true
FEATURE [Part::Feature] Face001
  shape: bbox 15.35 x 15.44 x 18.51 mm, 1 faces, 0 solids (baked)
FEATURE [Part::Feature] Face002
  shape: bbox 3 x 1.961 x 4.493e-05 mm, 1 faces, 0 solids (baked)
FEATURE [Part::Extrusion] Extrude035
  Base = -> Face001
  Dir = (0,0,40)
  Placement = pos=(0,0,0.2) rot=(0,0,1;0rad)
  Solid = true
FEATURE [Part::Extrusion] Extrude036
  Base = -> Face002
  Dir = (0,0,40)
  Solid = true
FEATURE [Part::MultiFuse] Fusion059
  Shapes = -> [Extrude034,Extrude036,Extrude035]
FEATURE [Sketcher::SketchObject] Sketch041
  Placement = pos=(-83,-8,40) rot=(1,0,0;3.14159rad)
  Support = -> Box018 [Face5]
  sketch-geometry (6):
    g0: ArcOfCircle CenterX=36.3668 CenterY=5.40677 CenterZ=0 NormalX=0 NormalY=0 NormalZ=1 Radius=21.3229 StartAngle=3.54834 EndAngle=4.6743
    g1: LineSegment StartX=4.75486 StartY=-2.01911 StartZ=0 EndX=16.7836 EndY=-3.02908 EndZ=0
    g2: LineSegment StartX=35.5549 StartY=-27.8711 StartZ=0 EndX=35.5549 EndY=-15.9007 EndZ=0
    g3: LineSegment StartX=-0.0196707 StartY=-6.40957 StartZ=0 EndX=-0.0196707 EndY=-18.9102 EndZ=0
    g4: ArcOfCircle CenterX=4.38623 CenterY=-6.40957 CenterZ=0 NormalX=0 NormalY=0 NormalZ=1 Radius=4.4059 StartAngle=1.48703 EndAngle=3.14159
    g5: ArcOfCircle CenterX=54.5601 CenterY=122.674 CenterZ=0 NormalX=0 NormalY=0 NormalZ=1 Radius=151.74 StartAngle=4.34445 EndAngle=4.58681
  constraints (8):
    c: Coincident(g1,g0)
    c: Coincident(g2,g0)
    c: Vertical(g3)
    c: Tangent(g3,g4)
    c: Tangent(g1,g4)
    c: Coincident(g5,g3)
    c: Coincident(g5,g2)
    c: Vertical(g2)
FEATURE [Part::Extrusion] Extrude037
  Base = -> Sketch041
  Dir = (0,0,-41.5)
  Placement = pos=(0,0,-0.15) rot=(0,0,1;0rad)
  Solid = true
FEATURE [Part::Cut] Cut051  label="support"
  Base = -> Fusion059
  Tool = -> Box018
FEATURE [Part::Box] Box019  label="Cube"
  Height = 8
  Length = 3
  Placement = pos=(-50,9.9,30) rot=(0,0,1;0rad)
  Width = 8
FEATURE [Part::Thickness] Thickness
  Faces = -> Extrude037 [Face8]
  Intersection = false
  Join = 2
  Mode = 0
  SelfIntersection = false
  Value = 0.15
FEATURE [Part::Cut] Cut052  label="chamber"
  Base = -> Thickness
  Tool = -> Box019
FEATURE [Part::Mirroring] Part__Mirroring009  label="support (Mirror #4)"
  Base = (0,0,0)
  Normal = (1,0,0)
  Source = -> Cut051
FEATURE [Part::MultiFuse] Fusion060  label="support001"
  Placement = pos=(0,0,0) rot=(0,1,0;3.14159rad)
  Shapes = -> [Part__Mirroring009,Cut051]
FEATURE [Part::Feature] Face003
  shape: bbox 26.93 x 10.39 x 11.36 mm, 1 faces, 0 solids (baked)
FEATURE [Part::Feature] Face004
  shape: bbox 35 x 20.89 x 2e-07 mm, 1 faces, 0 solids (baked)
FEATURE [Part::Extrusion] Extrude038
  Base = -> Face003
  Dir = (0,0,5)
  Solid = true
FEATURE [Part::Extrusion] Extrude039
  Base = -> Face004
  Dir = (0,0,5)
  Solid = true
FEATURE [Part::MultiFuse] Fusion062
  Shapes = -> [Extrude038,Extrude039]
FEATURE [Part::MultiCommon] Common014
  Shapes = -> [Fusion062,Extrude020]
FEATURE [Part::MultiCommon] Common015  label="cap001"
  Shapes = -> [Common014,Extrude019]
FEATURE [Part::Cut] Cut053  label="cap002"
  Base = -> Common015
  Tool = -> Extrude029
FEATURE [Part::MultiFuse] Fusion063  label="cap003"
  Shapes = -> [Cut053,Cut022]
FEATURE [Part::Cut] Cut054  label="cap004"
  Base = -> Fusion063
  Tool = -> Fusion044
FEATURE [Part::Mirroring] Part__Mirroring010  label="chamber (Mirror #4)"
  Base = (0,0,0)
  Normal = (1,0,0)
  Source = -> Cut052
FEATURE [Part::MultiFuse] Fusion064  label="chamber001"
  Placement = pos=(0,0,0) rot=(0,1,0;3.14159rad)
  Shapes = -> [Part__Mirroring010,Cut052]
FEATURE [Part::Mirroring] Part__Mirroring012  label="cap004 (Mirror #5)"
  Base = (0,0,0)
  Normal = (1,0,0)
  Source = -> Cut054
FEATURE [Part::MultiFuse] Fusion072  label="cap005"
  Shapes = -> [Part__Mirroring012,Cut054]
FEATURE [Part::Extrusion] Extrude040
  Base = -> Face004
  Dir = (0,0,5)
  Solid = true
FEATURE [Part::Offset] Offset001
  Fill = false
  Intersection = false
  Join = 2
  Mode = 0
  SelfIntersection = false
  Source = -> Extrude040
  Value = 3
FEATURE [Part::Offset] Offset002
  Fill = false
  Intersection = false
  Join = 2
  Mode = 0
  Placement = pos=(0,0,-0.15) rot=(0,0,1;0rad)
  SelfIntersection = false
  Source = -> Extrude040
  Value = 3
FEATURE [Part::Cut] Cut059  label="capStand"
  Base = -> Offset001
  Placement = pos=(0,0,-7.85) rot=(0,0,1;0rad)
  Tool = -> Offset002
FEATURE [Part::MultiFuse] Fusion073
  Shapes = -> [Loft003,Loft002,Fusion006]
FEATURE [Part::Cut] Cut060  label="capStand001"
  Base = -> Cut059
  Tool = -> Fusion073
FEATURE [Part::Mirroring] Part__Mirroring013  label="capStand001 (Mirror #6)"
  Base = (0,0,0)
  Normal = (1,0,0)
  Source = -> Cut060
FEATURE [Part::MultiFuse] Fusion075  label="capStand002"
  Shapes = -> [Cut060,Part__Mirroring013]
FEATURE [Sketcher::SketchObject] Sketch044
  Placement = pos=(0,0,40) rot=(1,0,0;3.14159rad)
  sketch-geometry (2):
    g0: Circle CenterX=-17.5 CenterY=-11.2 CenterZ=0 NormalX=0 NormalY=0 NormalZ=1 Radius=1.8
    g1: Circle CenterX=-7.5 CenterY=-4.2 CenterZ=0 NormalX=0 NormalY=0 NormalZ=1 Radius=1.8
  constraints (6):
    c: Radius(g0) = 1.8
    c: DistanceX(g0) = -17.5
    c: DistanceY(g0) = -11.2
    c: DistanceY(g0,g1) = 7
    c: DistanceX(g1,g0) = -10
    c: Radius(g1) = 1.8
FEATURE [Part::Extrusion] Extrude042
  Base = -> Sketch044
  Dir = (0,0,2)
  Solid = true
FEATURE [Part::Mirroring] Part__Mirroring014  label="Extrude042 (Mirror #7)"
  Base = (0,0,0)
  Normal = (1,0,0)
  Source = -> Extrude042
FEATURE [Part::MultiFuse] Fusion076  label="capScrew"
  Shapes = -> [Part__Mirroring014,Extrude042]
FEATURE [Part::FeaturePython] Facebinder006  # WARN: FeaturePython — macro-defined, semantics opaque (R4)
  Faces = -> [Common001]
FEATURE [Part::Extrusion] Extrude043
  Base = -> Facebinder006
  Dir = (0,5,0)
  Solid = true
FEATURE [Sketcher::SketchObject] Sketch045
  Placement = pos=(0,0,0) rot=(0.57735,0.57735,0.57735;2.0944rad)
  sketch-geometry (6):
    g0: LineSegment StartX=-2.39218 StartY=34 StartZ=0 EndX=15.0502 EndY=34 EndZ=0
    g1: LineSegment StartX=15.0502 StartY=34 StartZ=0 EndX=15.0502 EndY=31.0195 EndZ=0
    g2: ArcOfCircle CenterX=6.25655 CenterY=19.9033 CenterZ=0 NormalX=0 NormalY=0 NormalZ=1 Radius=16.5384 StartAngle=2.1211 EndAngle=2.72907
    g3: ArcOfCircle CenterX=-1.62233 CenterY=23.3513 CenterZ=0 NormalX=0 NormalY=0 NormalZ=1 Radius=7.93803 StartAngle=2.72907 EndAngle=3.409
    g4: ArcOfCircle CenterX=-13.9989 CenterY=61.1559 CenterZ=0 NormalX=0 NormalY=0 NormalZ=1 Radius=41.8575 StartAngle=4.86992 EndAngle=5.47942
    g5: ArcOfCircle CenterX=-7.68362 CenterY=21.3979 CenterZ=0 NormalX=0 NormalY=0 NormalZ=1 Radius=1.60111 StartAngle=3.23169 EndAngle=4.86992
  constraints (14):
    c: Horizontal(g0)
    c: DistanceY(g0) = 34
    c: PointOnObject(g1,g0)
    c: Vertical(g1)
    c: Coincident(g2,g0)
    c: DistanceX(g1) = 15.0502
    c: Coincident(g3,g2)
    c: Tangent(g3,g2)
    c: Coincident(g0,g1)
    c: Coincident(g4,g1)
    c: Coincident(g5,g4)
    c: Coincident(g5,g3)
    c: Tangent(g5,g4)
    c: DistanceY(g1) = 31.0195
FEATURE [Part::Box] Box020  label="mic"
  Height = 5.6
  Length = 3.4
  Placement = pos=(-11.8,-5.39609,22.5303) rot=(0.791603,0.545128,-0.276046;0.466207rad)
  Width = 15.4
FEATURE [Part::Extrusion] Extrude044  label="nosePad"
  Base = -> Sketch045
  Dir = (-15,0,0)
  Solid = true
FEATURE [Part::FeaturePython] Facebinder007  # WARN: FeaturePython — macro-defined, semantics opaque (R4)
  Faces = -> [Extrude043]
FEATURE [Part::Extrusion] Extrude045
  Base = -> Facebinder007
  Dir = (0,0,-15)
  Solid = true
FEATURE [Part::MultiFuse] Fusion077
  Shapes = -> [Extrude043,Extrude045]
FEATURE [Part::Offset] Offset003  label="mic001"
  Fill = false
  Intersection = false
  Join = 2
  Mode = 0
  SelfIntersection = false
  Source = -> Box020
  Value = 0.8
FEATURE [Sketcher::SketchObject] Sketch047
  Placement = pos=(4.19032,-7.02848,17.0363) rot=(0.993516,0.022102,-0.111527;3.53041rad)
  Support = -> Offset003 [Face5]
  sketch-geometry (4):
    g0: ArcOfCircle CenterX=-147.273 CenterY=-34.1627 CenterZ=0 NormalX=0 NormalY=0 NormalZ=1 Radius=138.577 StartAngle=0.0409891 EndAngle=0.234252
    g1: ArcOfCircle CenterX=-146.967 CenterY=-43.9265 CenterZ=0 NormalX=0 NormalY=0 NormalZ=1 Radius=134.494 StartAngle=0.113774 EndAngle=0.29395
    g2: LineSegment StartX=-13.3417 StartY=-28.6575 StartZ=0 EndX=-8.81253 EndY=-28.4842 EndZ=0
    g3: ArcOfCircle CenterX=-14.881 CenterY=-4.41142 CenterZ=0 NormalX=0 NormalY=0 NormalZ=1 Radius=3.40439 StartAngle=0.788387 EndAngle=3.30307
  constraints (8):
    c: Coincident(g2,g1)
    c: Coincident(g2,g0)
    c: Coincident(g3,g1)
    c: Coincident(g3,g0)
    c: DistanceX(g0) = -12.4809
    c: DistanceY(g0) = -1.99697
    c: DistanceX(g1) = -13.3417
    c: DistanceY(g1) = -28.6575
FEATURE [PartDesign::Pad] Pad003
  Length = 30
  Length2 = 100
  Midplane = true
  Reversed = true
  Sketch = -> Sketch047
  Type = 0
FEATURE [Part::Box] Box021  label="Cube042"
  Height = 3.3
  Length = 8
  Placement = pos=(-7.5,-6,31) rot=(0,0,1;0rad)
  Width = 21
FEATURE [Part::FeaturePython] Facebinder008  # WARN: FeaturePython — macro-defined, semantics opaque (R4)
  Faces = -> [Common001]
FEATURE [Part::Extrusion] Extrude046
  Base = -> Facebinder008
  Dir = (0,0,-5)
  Solid = true
FEATURE [Part::MultiCommon] Common017
  Shapes = -> [Extrude046,Box021]
FEATURE [Part::Box] Box022  label="Cube043"
  Height = 4
  Length = 4.2
  Placement = pos=(-4.2,1.6,32) rot=(0,0,1;0rad)
  Width = 8.4
FEATURE [Sketcher::SketchObject] Sketch048
  Placement = pos=(0,0,31) rot=(1,0,0;3.14159rad)
  sketch-geometry (1):
    g0: Circle CenterX=-9 CenterY=-10 CenterZ=0 NormalX=0 NormalY=0 NormalZ=1 Radius=1.7
  constraints (3):
    c: Radius(g0) = 1.7
    c: DistanceX(g0) = -9
    c: DistanceY(g0) = -10
FEATURE [Sketcher::SketchObject] Sketch049
  Placement = pos=(0,0,33) rot=(1,0,0;3.14159rad)
  sketch-geometry (1):
    g0: Circle CenterX=-9 CenterY=-10 CenterZ=0 NormalX=0 NormalY=0 NormalZ=1 Radius=1.7
  constraints (3):
    c: Radius(g0) = 1.7
    c: DistanceX(g0) = -9
    c: DistanceY(g0) = -10
FEATURE [Sketcher::SketchObject] Sketch050
  Placement = pos=(0,0,34) rot=(1,0,0;3.14159rad)
  sketch-geometry (1):
    g0: Circle CenterX=-9 CenterY=-10 CenterZ=0 NormalX=0 NormalY=0 NormalZ=1 Radius=1
  constraints (3):
    c: Radius(g0) = 1
    c: DistanceX(g0) = -9
    c: DistanceY(g0) = -10
FEATURE [Sketcher::SketchObject] Sketch051
  Placement = pos=(0,0,36.5) rot=(1,0,0;3.14159rad)
  sketch-geometry (1):
    g0: Circle CenterX=-9 CenterY=-10 CenterZ=0 NormalX=0 NormalY=0 NormalZ=1 Radius=1
  constraints (3):
    c: Radius(g0) = 1
    c: DistanceX(g0) = -9
    c: DistanceY(g0) = -10
FEATURE [Part::Loft] Loft006
  Closed = false
  Placement = pos=(9,-11.5,-0.01) rot=(0,0,1;0rad)
  Ruled = true
  Sections = -> [Sketch048,Sketch049,Sketch050,Sketch051]
  Solid = true
FEATURE [Part::Box] Box023  label="Cube044"
  Height = 3.3
  Length = 13.5
  Placement = pos=(-13.5,6,31) rot=(0,0,1;0rad)
  Width = 20.8
FEATURE [Part::MultiCommon] Common019
  Shapes = -> [Box023,Extrude046]
FEATURE [Part::MultiFuse] Fusion078
  Shapes = -> [Common017,Common019]
FEATURE [Part::Box] Box024  label="Cube045"
  Height = 4
  Length = 4.2
  Placement = pos=(0.8,1.6,32) rot=(0,0,1;0rad)
  Width = 8.4
FEATURE [Sketcher::SketchObject] Sketch052
  Placement = pos=(-11.8,-5.39609,22.531) rot=(0.98964,-0.06486,-0.128083;3.50939rad)
  sketch-geometry (4):
    g0: LineSegment StartX=-15.0876 StartY=7.99911 StartZ=0 EndX=25.2035 EndY=7.99911 EndZ=0
    g1: LineSegment StartX=25.2035 StartY=7.99911 StartZ=0 EndX=25.2035 EndY=-27.4678 EndZ=0
    g2: LineSegment StartX=25.2035 StartY=-27.4678 StartZ=0 EndX=-15.0876 EndY=-27.4678 EndZ=0
    g3: LineSegment StartX=-15.0876 StartY=-27.4678 StartZ=0 EndX=-15.0876 EndY=7.99911 EndZ=0
  constraints (8):
    c: Coincident(g0,g1)
    c: Coincident(g1,g2)
    c: Coincident(g2,g3)
    c: Coincident(g3,g0)
    c: Horizontal(g0)
    c: Horizontal(g2)
    c: Vertical(g1)
    c: Vertical(g3)
FEATURE [PartDesign::Pad] Pad004
  Length = 10
  Length2 = 100
  Placement = pos=(-11.8,-5.39609,22.531) rot=(0.98964,-0.06486,-0.128083;3.50939rad)
  Sketch = -> Sketch052
  Type = 0
FEATURE [PartDesign::Pad] Pad
  Length = 30
  Length2 = 100
  Midplane = true
  Placement = pos=(-77.783,8.88483,0.000119934) rot=(0,0.708449,0.705762;3.26493rad)
  Sketch = -> Sketch023
  Type = 0
FEATURE [Part::FeaturePython] Facebinder009  # WARN: FeaturePython — macro-defined, semantics opaque (R4)
  Faces = -> [Common001]
FEATURE [Part::Extrusion] Extrude047
  Base = -> Facebinder009
  Dir = (1,0,-1)
  Solid = true
FEATURE [Part::Box] Box025  label="Cube046"
  Height = 27
  Length = 10
  Placement = pos=(-69.7,-1.1,8) rot=(0,0,1;0rad)
  Width = 11
FEATURE [Part::MultiCommon] Common021  label="coverExtra001"
  Shapes = -> [Box025,Extrude047]
FEATURE [Part::MultiFuse] Fusion099  label="coverExtra002"
  Shapes = -> [Common021,Cut018]
FEATURE [Mesh::Feature] coverExtraFlat
FEATURE [Part::Feature] Shape002  label="coverExtraFlat001"
  shape: bbox 42.86 x 13.11 x 2e-07 mm, 31 faces, 0 solids (baked)
FEATURE [Part::FeaturePython] Facebinder010  # WARN: FeaturePython — macro-defined, semantics opaque (R4)
  Faces = -> [Fusion099]
FEATURE [Part::Extrusion] Extrude048  label="coverExtraflat"
  Base = -> Shape002
  Dir = (0,0,1)
  Solid = true
FEATURE [Part::Extrusion] Extrude049
  Base = -> Facebinder010
  Dir = (0,0,1)
  Solid = true
FEATURE [Part::MultiFuse] Fusion100  label="coverExtraflat001"
  Shapes = -> [Extrude048,Extrude049]
FEATURE [Part::MultiFuse] Fusion101  label="coverExtraFlat002"
  Shapes = -> [Cut012,Fusion100]
FEATURE [Part::MultiFuse] Fusion102  label="flatClips"
  Shapes = -> [Sphere008,Sphere010,Sphere011,Sphere012,Sphere013,Sphere014,Sphere015]
FEATURE [Part::MultiFuse] Fusion104  label="clips"
  Shapes = -> [Sphere006,Sphere002,Sphere003,Sphere004,Sphere,Sphere001,Sphere007]
FEATURE [Part::Box] Box026  label="Cube047"
  Height = 27
  Length = 10
  Placement = pos=(-69.7,-1.1,6.5) rot=(0,0,1;0rad)
  Width = 11
FEATURE [Part::MultiCommon] Common022  label="coverExtraCut"
  Shapes = -> [Extrude047,Box026]
FEATURE [Part::FeaturePython] Facebinder011  # WARN: FeaturePython — macro-defined, semantics opaque (R4)
  Faces = -> [Common022]
FEATURE [Part::Extrusion] Extrude050  label="coverExtraCut001"
  Base = -> Facebinder011
  Dir = (-1.1,0,1.1)
  Solid = true
FEATURE [Part::MultiFuse] Fusion108  label="trunk004"
  Shapes = -> [Fusion104,Cut010,Common004,Fusion007,Cut042,Cut043]
FEATURE [Part::Box] Box027  label="Cube048"
  Height = 11
  Length = 6
  Placement = pos=(-69.7,9.1,3.5) rot=(0,0,1;0rad)
  Width = 10
FEATURE [Part::Cut] Cut076  label="coverExtraCut002"
  Base = -> Extrude050
  Tool = -> Box027
FEATURE [Mesh::Feature] coverExtra  label="coverExtra003"
FEATURE [Part::Feature] Shape003  label="coverExtra004"
  shape: bbox 66.18 x 18.13 x 26 mm, 52 faces, 0 solids (baked)
FEATURE [Sketcher::SketchObject] Sketch054
  Placement = pos=(0,0,36.5) rot=(1,0,0;3.14159rad)
  sketch-geometry (1):
    g0: Circle CenterX=-9 CenterY=-10 CenterZ=0 NormalX=0 NormalY=0 NormalZ=1 Radius=0.6
  constraints (3):
    c: Radius(g0) = 0.6
    c: DistanceX(g0) = -9
    c: DistanceY(g0) = -10
FEATURE [Sketcher::SketchObject] Sketch055
  Placement = pos=(0,0,34) rot=(1,0,0;3.14159rad)
  sketch-geometry (1):
    g0: Circle CenterX=-9 CenterY=-10 CenterZ=0 NormalX=0 NormalY=0 NormalZ=1 Radius=0.6
  constraints (3):
    c: Radius(g0) = 0.6
    c: DistanceX(g0) = -9
    c: DistanceY(g0) = -10
FEATURE [Sketcher::SketchObject] Sketch056
  Placement = pos=(0,0,33) rot=(1,0,0;3.14159rad)
  sketch-geometry (1):
    g0: Circle CenterX=-9 CenterY=-10 CenterZ=0 NormalX=0 NormalY=0 NormalZ=1 Radius=1.3
  constraints (3):
    c: Radius(g0) = 1.3
    c: DistanceX(g0) = -9
    c: DistanceY(g0) = -10
FEATURE [Part::Loft] Loft008
  Closed = false
  Placement = pos=(-67,-4.5,0) rot=(0,0,1;0rad)
  Ruled = true
  Sections = -> [Sketch056,Sketch055,Sketch054]
  Solid = true
FEATURE [Sketcher::SketchObject] Sketch057
  Placement = pos=(0,0,34) rot=(1,0,0;3.14159rad)
  sketch-geometry (4):
    g0: LineSegment StartX=-69.2498 StartY=-8.24146 StartZ=0 EndX=-62.1203 EndY=-1.44791 EndZ=0
    g1: LineSegment StartX=-69.2498 StartY=-8.24146 StartZ=0 EndX=-77.7946 EndY=-2.11025 EndZ=0
    g2: LineSegment StartX=-77.7946 StartY=-2.11025 StartZ=0 EndX=-64.0631 EndY=1.91909 EndZ=0
    g3: ArcOfCircle CenterX=-63.5 CenterY=0 CenterZ=0 NormalX=0 NormalY=0 NormalZ=1 Radius=2 StartAngle=5.47367 EndAngle=8.1394
  constraints (9):
    c: Coincident(g2,g1)
    c: Coincident(g3,g2)
    c: Coincident(g3,g0)
    c: Tangent(g2,g3)
    c: Tangent(g3,g0)
    c: Coincident(g1,g0)
    c: Radius(g3) = 2
    c: DistanceX(g3) = -63.5
    c: PointOnObject(g3,g-1)
FEATURE [Part::Extrusion] Extrude051  label="hinge"
  Base = -> Sketch057
  Dir = (0,0,1)
  Solid = true
FEATURE [Sketcher::SketchObject] Sketch058
  Placement = pos=(0,0,35) rot=(0,0,1;0rad)
  Support = -> Extrude051 [Face6]
  sketch-geometry (2):
    g0: Circle CenterX=-63.5 CenterY=0 CenterZ=0 NormalX=0 NormalY=0 NormalZ=1 Radius=2
    g1: LineSegment [constr] StartX=-58.5511 StartY=1.75491 StartZ=0 EndX=-58.5511 EndY=-7.02478 EndZ=0
  constraints (4):
    c: DistanceY(g0) = 0
    c: DistanceX(g0) = -63.5
    c: Radius(g0) = 2
    c: Vertical(g1)
FEATURE [PartDesign::Revolution] Revolution  label="hingeLeft"
  Angle = 20
  Axis = (0,-8.77969,0)
  Base = (-58.5511,1.75491,35)
  ReferenceAxis = -> Sketch058 [Axis0]
  Reversed = true
  Sketch = -> Sketch058
FEATURE [PartDesign::Revolution] Revolution001  label="hingeRight"
  Angle = 30
  Axis = (0,-8.77969,0)
  Base = (-58.5511,1.75491,35)
  ReferenceAxis = -> Sketch058 [Axis0]
  Reversed = true
  Sketch = -> Sketch058
FEATURE [Part::MultiCommon] Common023  label="nosePad001"
  Shapes = -> [Extrude044,Pad003]
FEATURE [Part::Fillet] Fillet
  Base = -> Common023
  Edges = 2 edges: [Edge6 r1=5 r2=2,Edge12 r=2]
FEATURE [Part::Fillet] Fillet003  label="nosePad002"
  Base = -> Fillet
  Edges = 1 edges r=2: [Edge21]
FEATURE [Part::MultiCommon] Common024  label="nosePadCover"
  Shapes = -> [Fillet003,Pad004]
FEATURE [Part::Fillet] Fillet004  label="nosePad003"
  Base = -> Fillet
  Edges = 1 edges r=2: [Edge21]
  Placement = pos=(-5.28091,0,-1.77323) rot=(0,1,0;0.20944rad)
FEATURE [Part::Cut] Cut081  label="nosePad004"
  Base = -> Fillet004
  Tool = -> Fusion077
FEATURE [Part::Fillet] Fillet005  label="nosePad005"
  Base = -> Cut081
  Edges = 2 edges r=1.5: [Edge10,Edge31]
FEATURE [Part::Fillet] Fillet006
  Base = -> Fusion078
  Edges = 3 edges r=2: [Edge3,Edge30,Edge31]
FEATURE [Part::Fillet] Fillet007
  Base = -> Fillet006
  Edges = 1 edges r=1: [Edge19]
FEATURE [Part::MultiFuse] Fusion115  label="nosePad006"
  Shapes = -> [Fillet005,Fillet007]
FEATURE [Sketcher::SketchObject] Sketch059
  ExternalGeometry = -> [Box020]
  Placement = pos=(-11.8,-5.39609,22.5303) rot=(0.98964,-0.06486,-0.128083;3.50938rad)
  Support = -> Box020 [Face5]
  sketch-geometry (1):
    g0: Circle CenterX=1 CenterY=-15.4 CenterZ=0 NormalX=0 NormalY=0 NormalZ=1 Radius=1
  constraints (3):
    c: PointOnObject(g0,g-3)
    c: Radius(g0) = 1
    c: PointOnObject(g-3,g0)
FEATURE [PartDesign::Pad] Pad006
  Length = 5.6
  Length2 = 100
  Placement = pos=(-11.8,-5.39609,22.5303) rot=(0.791603,0.545128,-0.276046;0.466207rad)
  Reversed = true
  Sketch = -> Sketch059
  Type = 0
FEATURE [Part::MultiFuse] Fusion116
  Placement = pos=(-5.28091,0,-1.77323) rot=(0,1,0;0.20944rad)
  Shapes = -> [Pad006,Pad004]
FEATURE [Sketcher::SketchObject] Sketch060
  ExternalGeometry = -> [Fusion116]
  Placement = pos=(4.94731,-9.40855,19.3675) rot=(0.678048,0.735002,0.004792;0.581549rad)
  Support = -> Fusion116 [Face1]
  sketch-geometry (1):
    g0: Circle CenterX=-12.9087 CenterY=18.5936 CenterZ=0 NormalX=0 NormalY=0 NormalZ=1 Radius=1
  constraints (2):
    c: Coincident(g0,g-3)
    c: Equal(g0,g-3)
FEATURE [Part::Extrusion] Extrude052
  Base = -> Sketch060
  Dir = (-0.5,0,4)
  Solid = true
FEATURE [Part::MultiFuse] Fusion117
  Shapes = -> [Extrude052,Fusion116]
FEATURE [Part::Loft] Loft009
  Closed = false
  Placement = pos=(-1.5,1.2,-0.01) rot=(0,0,1;0rad)
  Ruled = true
  Sections = -> [Sketch048,Sketch049,Sketch050,Sketch051]
  Solid = true
FEATURE [Part::MultiFuse] Fusion118
  Shapes = -> [Loft006,Loft009,Box022]
FEATURE [Part::Cut] Cut082  label="nosePad007"
  Base = -> Fusion115
  Tool = -> Fusion118
FEATURE [Part::Mirroring] Part__Mirroring  label="nosePad007 (Mirror #9)"
  Base = (0,0,0)
  Normal = (1,0,0)
  Source = -> Cut082
FEATURE [Part::Cut] Cut083  label="nosePadLeft"
  Base = -> Part__Mirroring
  Tool = -> Box024
FEATURE [Part::Cut] Cut084  label="nosePadRight"
  Base = -> Cut082
  Tool = -> Fusion117
FEATURE [Part::MultiFuse] Fusion119  label="nosePad008"
  Placement = pos=(0,0,0) rot=(0,1,0;3.14159rad)
  Shapes = -> [Cut083,Cut084]
FEATURE [Part::MultiFuse] Fusion120
  Shapes = -> [Loft009,Loft006,Loft008,Fusion006,Fusion102]
FEATURE [Part::Cut] Cut085  label="coverExtraFlat003"
  Base = -> Fusion101
  Tool = -> Fusion120
FEATURE [Part::Mirroring] Part__Mirroring018  label="coverExtraFlat003 (Mirror #9)"
  Base = (0,0,0)
  Normal = (1,0,0)
  Source = -> Cut085
FEATURE [Part::Cut] Cut086  label="coverExtraFlatRight"
  Base = -> Cut085
  Tool = -> Extrude052
FEATURE [Part::MultiFuse] Fusion121  label="coverExtraFlat004"
  Shapes = -> [Part__Mirroring018,Cut086]
FEATURE [Part::Mirroring] Part__Mirroring019  label="hingeRight (Mirror #9)"
  Base = (0,0,0)
  Normal = (1,0,0)
  Source = -> Revolution001
FEATURE [Part::FeaturePython] Facebinder012  # WARN: FeaturePython — macro-defined, semantics opaque (R4)
  Faces = -> [Cut076]
FEATURE [Part::Extrusion] Extrude053
  Base = -> Facebinder012
  Dir = (0,-5,2)
  Solid = true
FEATURE [Part::MultiFuse] Fusion122  label="pockets"
  Shapes = -> [Loft002,Loft003,Loft006,Pad002,Fusion006,Cut012,Extrude009,Box010,Fusion014,Cut076,Extrude053,Pad]
FEATURE [Part::Cut] Cut087  label="trunk005"
  Base = -> Fusion108
  Tool = -> Fusion122
FEATURE [Part::MultiFuse] Fusion123  label="coverExtraFlat005"
  Shapes = -> [Part__Mirroring019,Revolution,Fusion121]
FEATURE [Part::Fillet] Fillet008  label="trunk006"
  Base = -> Cut087
  Edges = 3 edges: [Edge107 r=3,Edge273 r=1,Edge361 r=1]
FEATURE [Part::Mirroring] Part__Mirroring020  label="trunk006 (Mirror #9)"
  Base = (0,0,0)
  Normal = (1,0,0)
  Source = -> Fillet008
FEATURE [Part::MultiFuse] Fusion124  label="trunk007"
  Placement = pos=(0,0,0) rot=(0,1,0;3.14159rad)
  Shapes = -> [Part__Mirroring020,Fillet008]
FEATURE [Part::Box] Box028  label="Cube049"
  Height = 11
  Length = 165
  Placement = pos=(-82,-11,-44) rot=(0,0,1;0rad)
  Width = 48
FEATURE [Part::Cut] Cut088  label="trunk008"
  Base = -> Fusion124
  Tool = -> Box028
